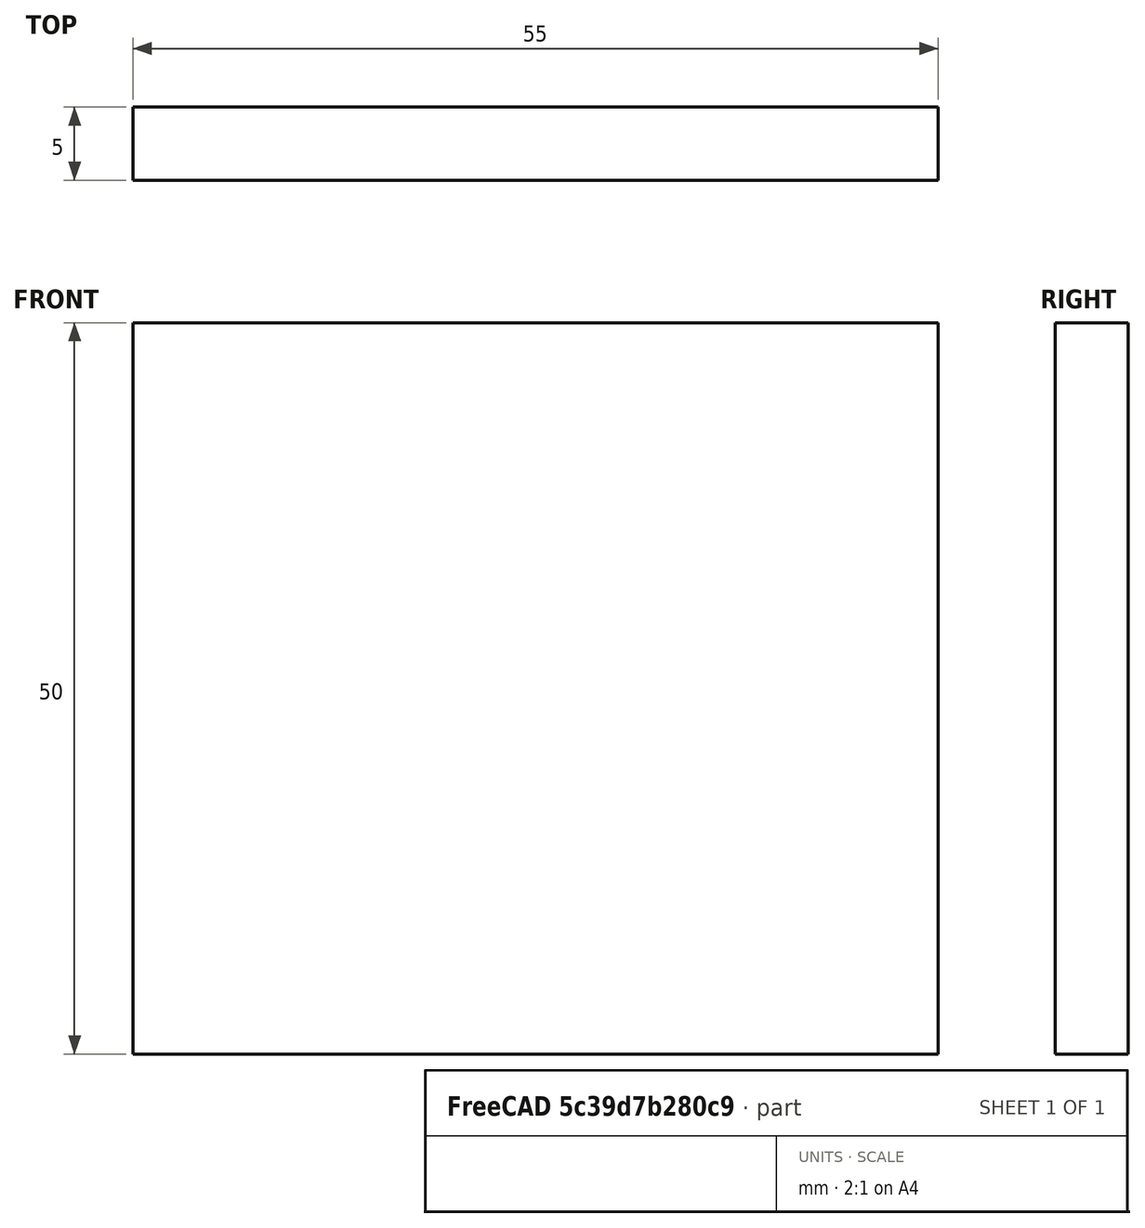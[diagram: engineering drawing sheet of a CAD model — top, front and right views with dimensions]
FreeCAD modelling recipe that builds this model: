
FCSTD DOCUMENT  (FreeCAD 0.15R4671 (Git))
Label: Flat Bar 55x5 EN10058 S235JR
License: All rights reserved
LicenseURL: http://en.wikipedia.org/wiki/All_rights_reserved
objects: Sketcher::SketchObject×1, Part::Extrusion×1
note: 2 computed .brp shape members not serialized (recipe doc carries the construction recipe); baked Part::Feature solids carry a one-line shape summary decoded from their .brp

FEATURE [Sketcher::SketchObject] Sketch
  sketch-geometry (4):
    g0: LineSegment StartX=-27.5 StartY=-2.5 StartZ=0 EndX=27.5 EndY=-2.5 EndZ=0
    g1: LineSegment StartX=27.5 StartY=-2.5 StartZ=0 EndX=27.5 EndY=2.5 EndZ=0
    g2: LineSegment StartX=27.5 StartY=2.5 StartZ=0 EndX=-27.5 EndY=2.5 EndZ=0
    g3: LineSegment StartX=-27.5 StartY=2.5 StartZ=0 EndX=-27.5 EndY=-2.5 EndZ=0
  constraints (12):
    c: Coincident(g0,g1)
    c: Coincident(g1,g2)
    c: Coincident(g2,g3)
    c: Coincident(g3,g0)
    c: Horizontal(g0)
    c: Horizontal(g2)
    c: Vertical(g1)
    c: Vertical(g3)
    c: Symmetric(g1,g2,g-2)
    c: Symmetric(g0,g1,g-1)
    c: DistanceY(g1) = 5
    c: DistanceX(g0) = 55
FEATURE [Part::Extrusion] Extrude  label="Flat Bar 55x5 EN10058 S235JR"
  Base = -> Sketch
  Dir = (0,0,50)
  Solid = true
